# Revit family: HERZ Kit For Connection Of Water Meters 4126
name_source: partatom
category: Rohrzubehör
units: mm (PartAtom-declared; Revit-internal decimal feet)

## family parameters
Arbeitsebenenbasiert = Nein
Beim Laden mit Abzugskörper schneiden = Nein
Bemaßung runder Anschluss = Durchmesser verwenden
Gemeinsam genutzt = Nein
Immer vertikal = Ja
OmniClass-Nummer = 23.65.55.14
OmniClass-Titel = Valves for Liquid Services
Teiletyp = Unterbricht

## types (1)
- HERZ Kit For Connection Of Water Meters 4126
    Application = The connection kit is used for mounting the water meter free of any tension or mechanical forces.
The HERZ – Kit for connection of water meters fulfills the requirements according to DIN 1988.
    Body = DZR brass CC752S
    Bracket = galvanized sheet steel
    Connections = DZR brass CW262N
    Hand wheel = plastic, green
    Hersteller = HERZ Armaturen Ges.m.b.H.
    L15 = 2 mm  [stored 0.00656168 ft]
    Max. differential pressure on closed seat = 1000000.0 Pa
    Max. operating pressure = 1600000.0 Pa
    Max. operating temperature = 80 °C
    Medium = Water
    Note = Pursuant to Article 33 of the REACH Regulation (EC No. 1907/2006), we are obliged to point out that the material lead is listed on the SVHC list and that all brass components manufactured in our products exceed 0.1% (w / w) lead (CAS: 7439-92-1 / EINECS: 231-100-4).
Since lead is a component part of an alloy, actual exposure is not possible and therefore no additional information on safe use is necessary.
    Occasional temperature rises = up to 95°C, if they do not last longer than 1 h
    Operating pressure from the backflow preventer = acc. to DIN EN 13959
    R50 = 4 mm  [stored 0.0131234 ft]
    S = 3 mm  [stored 0.00984252 ft]
    S03 = 10 mm  [stored 0.0328084 ft]
    SCTWCODE = 02;01;02
    SCTWSEQ = AW;SBT_TYP_AW="105";2
    SC_NennweiteBerechnet = 0
    Sealing = physiologically harmless material acc. to KTW
    Spindle seals = double O-Ring
    Spring = stainless steel 1.4310
    T01 = 3 mm  [stored 0.00984252 ft]
    T02 = 17 mm  [stored 0.0557743 ft]
    URL = www.herzvalves.com
    Upper part = DZR brass CC752S
    W01 = 20.00°

note: [stored X ft] marks values corroborated as IEEE doubles in the binary element streams (Revit-internal decimal feet)
